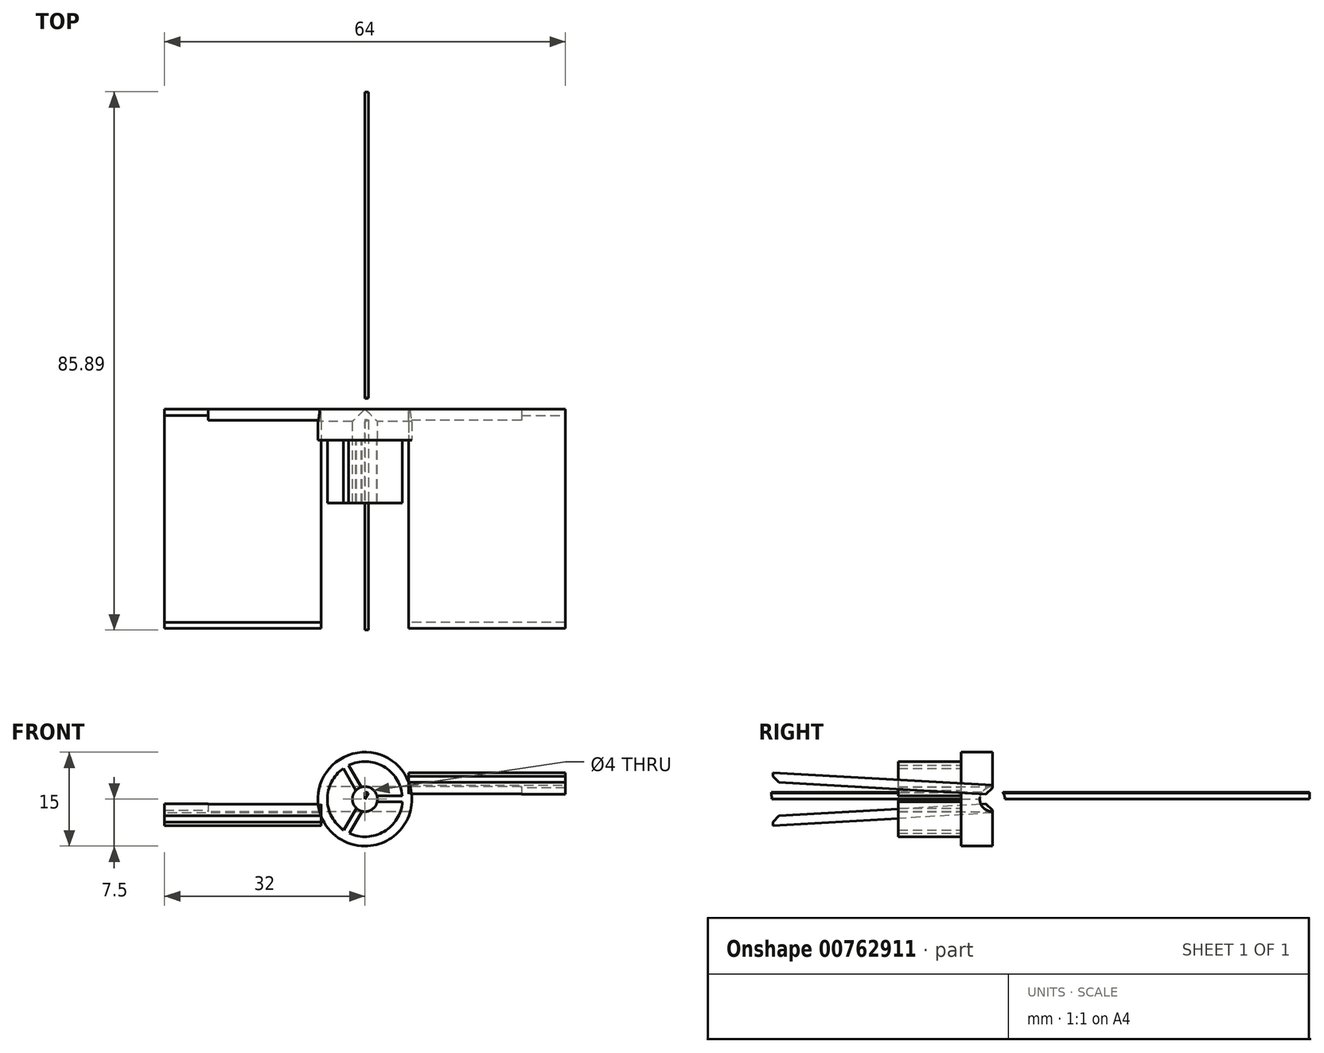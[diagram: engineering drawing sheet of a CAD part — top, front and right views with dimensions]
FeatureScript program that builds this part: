
annotation { "Feature Type Name" : "Feature", "Feature Type Description" : "" }
export const myFeature = defineFeature(function(context is Context, id is Id, definition is map)
    precondition{}
    {
        {
            var Q0;
            Q0=qCreatedBy(makeId("Front.planeOp"),FACE);
            var sketch = newSketch(context, id + "F0", { "sketchPlane" : qUnion([Q0])});
            skCircle(sketch, "E0", {"center": v(0, 0) * mm, "radius": 6 * mm});
            skCircle(sketch, "E1", {"center": v(0, 0) * mm, "radius": 7.5 * mm});
            skCircle(sketch, "E2", {"center": v(0, 0) * mm, "radius": 2 * mm});
            skCircle(sketch, "E3", {"center": v(0, 0) * mm, "radius": 5.1 * mm});
            skSolve(sketch);
        }
        {
            var Q0;
            Q0=makeQuery(id+"F0.imprint","IMPRINT",FACE,{"disambiguationData":[TD([[makeQuery(id+"F0.imprint","IMPRINT",EDGE,{"derivedFrom":sQuery(id+"F0.wireOp",EDGE,"E0")}),1.0]])]});
            var Q1;
            Q1=makeQuery(id+"F0.imprint","IMPRINT",FACE,{"disambiguationData":[TD([[makeQuery(id+"F0.imprint","IMPRINT",EDGE,{"derivedFrom":sQuery(id+"F0.wireOp",EDGE,"E2")}),-1.0]])]});
            extrude(context, id + "F1", {"entities" : qUnion([Q0, Q1]), "depth" : 10 * mm, "offsetDistance" : 25 * mm, "hasSecondDirection" : true, "secondDirectionOppositeDirection" : true, "secondDirectionDepth" : 5 * mm});
        }
        {
            var Q0;
            Q0=makeQuery(id+"F0.imprint","IMPRINT",FACE,{"disambiguationData":[TD([[makeQuery(id+"F0.imprint","IMPRINT",EDGE,{"derivedFrom":sQuery(id+"F0.wireOp",EDGE,"E0")}),-1.0]])]});
            var Q1;
            Q1=makeQuery(id+"F0.imprint","IMPRINT",FACE,{"disambiguationData":[TD([[makeQuery(id+"F0.imprint","IMPRINT",EDGE,{"derivedFrom":sQuery(id+"F0.wireOp",EDGE,"E0")}),1.0]])]});
            extrude(context, id + "F2", {"entities" : qUnion([Q0, Q1]), "operationType" : NewBodyOperationType.ADD, "oppositeDirection" : true, "depth" : 5 * mm, "offsetDistance" : 25 * mm});
        }
        {
            var Q0;
            Q0=qCreatedBy(makeId("Front.planeOp"),FACE);
            var sketch = newSketch(context, id + "F3", { "sketchPlane" : qUnion([Q0])});
            skLineSegment(sketch, "E4.bottom", {"start": v(0, 0.56) * mm, "end": v(7, 0.56) * mm});
            skLineSegment(sketch, "E4.top", {"start": v(0, -0.44) * mm, "end": v(7, -0.44) * mm});
            skLineSegment(sketch, "E4.left", {"start": v(0, 0.56) * mm, "end": v(0, -0.44) * mm});
            skLineSegment(sketch, "E4.right", {"start": v(7, 0.56) * mm, "end": v(7, -0.44) * mm});
            skLineSegment(sketch, "E5.1.0", {"start": v(-0.48, -0.28) * mm, "end": v(-3.98, 5.78) * mm});
            skLineSegment(sketch, "E5.1.1", {"start": v(-3.98, 5.78) * mm, "end": v(-3.12, 6.28) * mm});
            skLineSegment(sketch, "E5.1.2", {"start": v(0.38, 0.22) * mm, "end": v(-3.12, 6.28) * mm});
            skLineSegment(sketch, "E5.1.3", {"start": v(-0.48, -0.28) * mm, "end": v(0.38, 0.22) * mm});
            skLineSegment(sketch, "E5.2.0", {"start": v(0.48, -0.28) * mm, "end": v(-3.02, -6.34) * mm});
            skLineSegment(sketch, "E5.2.1", {"start": v(-3.02, -6.34) * mm, "end": v(-3.88, -5.84) * mm});
            skLineSegment(sketch, "E5.2.2", {"start": v(-0.38, 0.22) * mm, "end": v(-3.88, -5.84) * mm});
            skLineSegment(sketch, "E5.2.3", {"start": v(0.48, -0.28) * mm, "end": v(-0.38, 0.22) * mm});
            skPoint(sketch, "E5.center", {"position": v(0, 0) * mm});
            skSolve(sketch);
        }
        {
            var Q0;
            {var subQ0=sQuery(id+"F3.wireOp",EDGE,"E5.1.1");Q0=makeQuery(id+"F3.imprint","IMPRINT",FACE,{"disambiguationData":[TD([[makeQuery(id+"F3.imprint","IMPRINT",EDGE,{"derivedFrom":subQ0}),-1.0]])]});}
            var Q1;
            {var subQ5=sQuery(id+"F3.wireOp",EDGE,"E4.right");Q1=makeQuery(id+"F3.imprint","IMPRINT",FACE,{"disambiguationData":[TD([[makeQuery(id+"F3.imprint","IMPRINT",EDGE,{"derivedFrom":subQ5}),-1.0]])]});}
            var Q2;
            {var subQ5=sQuery(id+"F3.wireOp",EDGE,"E5.2.1");Q2=makeQuery(id+"F3.imprint","IMPRINT",FACE,{"disambiguationData":[TD([[makeQuery(id+"F3.imprint","IMPRINT",EDGE,{"derivedFrom":subQ5}),-1.0]])]});}
            extrude(context, id + "F4", {"entities" : qUnion([Q0, Q1, Q2]), "operationType" : NewBodyOperationType.REMOVE, "depth" : 25 * mm, "offsetDistance" : 25 * mm});
        }
        {
            var Q0;
            Q0=qCreatedBy(makeId("Front.planeOp"),FACE);
            var sketch = newSketch(context, id + "F5", { "sketchPlane" : qUnion([Q0])});
            skLineSegment(sketch, "E6.bottom", {"start": v(-7, -1) * mm, "end": v(-32, -1) * mm});
            skLineSegment(sketch, "E6.top", {"start": v(-7, -2.5) * mm, "end": v(-32, -2.5) * mm});
            skLineSegment(sketch, "E6.left", {"start": v(-7, -1) * mm, "end": v(-7, -2.5) * mm});
            skLineSegment(sketch, "E6.right", {"start": v(-32, -1) * mm, "end": v(-32, -2.5) * mm});
            skSolve(sketch);
        }
        {
            var Q0;
            Q0=qCreatedBy(makeId("Right.planeOp"),FACE);
            var sketch = newSketch(context, id + "F6", { "sketchPlane" : qUnion([Q0])});
            skLineSegment(sketch, "E7", {"start": v(-30, -0.73) * mm, "end": v(5, 1.27) * mm});
            skSolve(sketch);
        }
        {
            var Q0;
            Q0=makeQuery(id+"F5.imprint","IMPRINT",FACE,{"disambiguationData":[TD([[makeQuery(id+"F5.imprint","IMPRINT",EDGE,{"derivedFrom":sQuery(id+"F5.wireOp",EDGE,"E6.bottom")}),1.0]])]});
            var Q1;
            Q1=sQuery(id+"F6.wireOp",EDGE,"E7");
            sweep(context, id + "F7", {"profiles" : qUnion([Q0]), "path" : qUnion([Q1])});
        }
        {
            var Q0;
            Q0=qCreatedBy(makeId("Right.planeOp"),FACE);
            var sketch = newSketch(context, id + "F8", { "sketchPlane" : qUnion([Q0])});
            skLineSegment(sketch, "E8", {"start": v(-30.2, 0) * mm, "end": v(55.62, 0) * mm});
            skLineSegment(sketch, "E9", {"start": v(55.62, 0) * mm, "end": v(55.62, 1.11) * mm});
            skLineSegment(sketch, "E10", {"start": v(55.62, 1.11) * mm, "end": v(-30.27, 1.11) * mm});
            skLineSegment(sketch, "E11", {"start": v(-30.27, 1.11) * mm, "end": v(-30.2, 0) * mm});
            skSolve(sketch);
        }
        {
            var Q0;
            Q0=makeQuery(id+"F7.opSweep","CAP_EDGE",EDGE,{"disambiguationData":[OSD([sQuery(id+"F5.wireOp",EDGE,"E6.bottom"),sQuery(id+"F6.wireOp",VERTEX,"E7.start")])],"isStart":true});
            chamfer(context, id + "F9", {"entities" : qUnion([Q0]), "width" : 1 * mm, "tangentPropagation" : true});
        }
        {
            var Q0;
            Q0=makeQuery(id+"F8.imprint","IMPRINT",FACE,{"disambiguationData":[TD([[makeQuery(id+"F8.imprint","IMPRINT",EDGE,{"derivedFrom":sQuery(id+"F8.wireOp",EDGE,"E8")}),1.0]])]});
            var Q1;
            Q1=sQuery(id+"F8.wireOp",EDGE,"E8");
            revolve(context, id + "F10", {"surfaceOperationType" : NewSurfaceOperationType.NEW, "entities" : qUnion([Q0]), "axis" : qUnion([Q1]), "revolveType" : RevolveType.ONE_DIRECTION, "angle" : 30 * degree});
        }
        {
            var Q0;
            Q0=makeQuery(id+"F7.opSweep","CAP_EDGE",EDGE,{"disambiguationData":[OSD([sQuery(id+"F5.wireOp",EDGE,"E6.bottom"),sQuery(id+"F6.wireOp",VERTEX,"E7.start")])],"isStart":false});
            chamfer(context, id + "F11", {"entities" : qUnion([Q0]), "width" : 1 * mm, "tangentPropagation" : true});
        }
        {
            var Q0;
            Q0=makeQuery(id+"F7.opSweep","SWEPT_BODY",BODY,{"disambiguationData":[OSD([sQuery(id+"F5.wireOp",EDGE,"E6.bottom"),sQuery(id+"F5.wireOp",EDGE,"E6.top"),sQuery(id+"F5.wireOp",EDGE,"E6.left"),sQuery(id+"F5.wireOp",EDGE,"E6.right"),sQuery(id+"F6.wireOp",EDGE,"E7")])]});
            var Q1;
            Q1=makeQuery(id+"F10.opRevolve","CAP_EDGE",EDGE,{"disambiguationData":[OSD([sQuery(id+"F8.wireOp",EDGE,"E8")])],"isStart":true});
            circularPattern(context, id + "F12", {"entities" : qUnion([Q0]), "axis" : qUnion([Q1]), "angle" : 360 * degree, "instanceCount" : 2, "equalSpace" : true});
        }
        {
            var Q0;
            Q0=qCreatedBy(makeId("Right.planeOp"),FACE);
            var sketch = newSketch(context, id + "F13", { "sketchPlane" : qUnion([Q0])});
            skCircle(sketch, "E12", {"center": v(5, 0) * mm, "radius": 2 * mm});
            skSolve(sketch);
        }
        {
            var Q0;
            Q0 = qSketchRegion(id + "F13", true);
            extrude(context, id + "F14", {"entities" : qUnion([Q0]), "operationType" : NewBodyOperationType.REMOVE, "depth" : 25 * mm, "offsetDistance" : 25 * mm, "hasSecondDirection" : true, "secondDirectionOppositeDirection" : true, "secondDirectionDepth" : 25 * mm});
        }
    });
